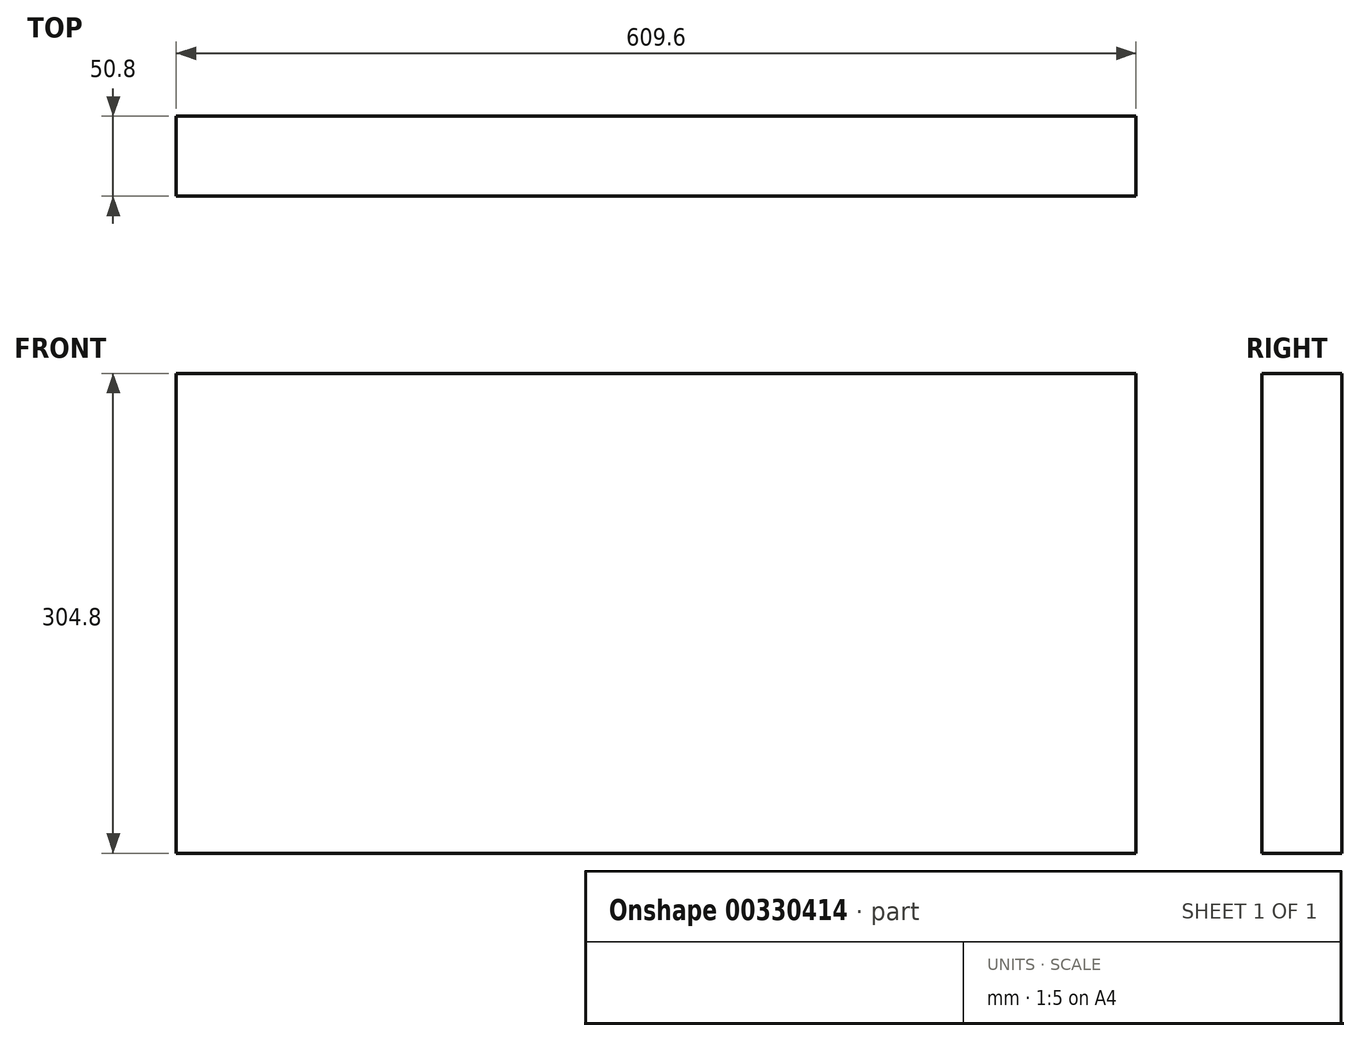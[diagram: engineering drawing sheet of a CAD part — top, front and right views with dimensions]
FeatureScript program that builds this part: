
annotation { "Feature Type Name" : "Feature", "Feature Type Description" : "" }
export const myFeature = defineFeature(function(context is Context, id is Id, definition is map)
    precondition{}
    {
        {
            var Q0;
            Q0=qCreatedBy(makeId("Front.planeOp"),FACE);
            var sketch = newSketch(context, id + "F0", { "sketchPlane" : qUnion([Q0])});
            skLineSegment(sketch, "E0", {"start": v(-299.37, 176.5) * mm, "end": v(310.23, 176.5) * mm});
            skLineSegment(sketch, "E1", {"start": v(310.23, 176.5) * mm, "end": v(310.23, -128.3) * mm});
            skLineSegment(sketch, "E2", {"start": v(310.23, -128.3) * mm, "end": v(-299.37, -128.3) * mm});
            skLineSegment(sketch, "E3", {"start": v(-299.37, -128.3) * mm, "end": v(-299.37, 176.5) * mm});
            skSolve(sketch);
        }
        {
            var Q0;
            Q0=makeQuery(id+"F0.imprint","IMPRINT",FACE,{"disambiguationData":[TD([[makeQuery(id+"F0.imprint","IMPRINT",EDGE,{"derivedFrom":sQuery(id+"F0.wireOp",EDGE,"E0")}),-1.0]])]});
            extrude(context, id + "F1", {"entities" : qUnion([Q0]), "depth" : 50.8 * mm});
        }
    });
